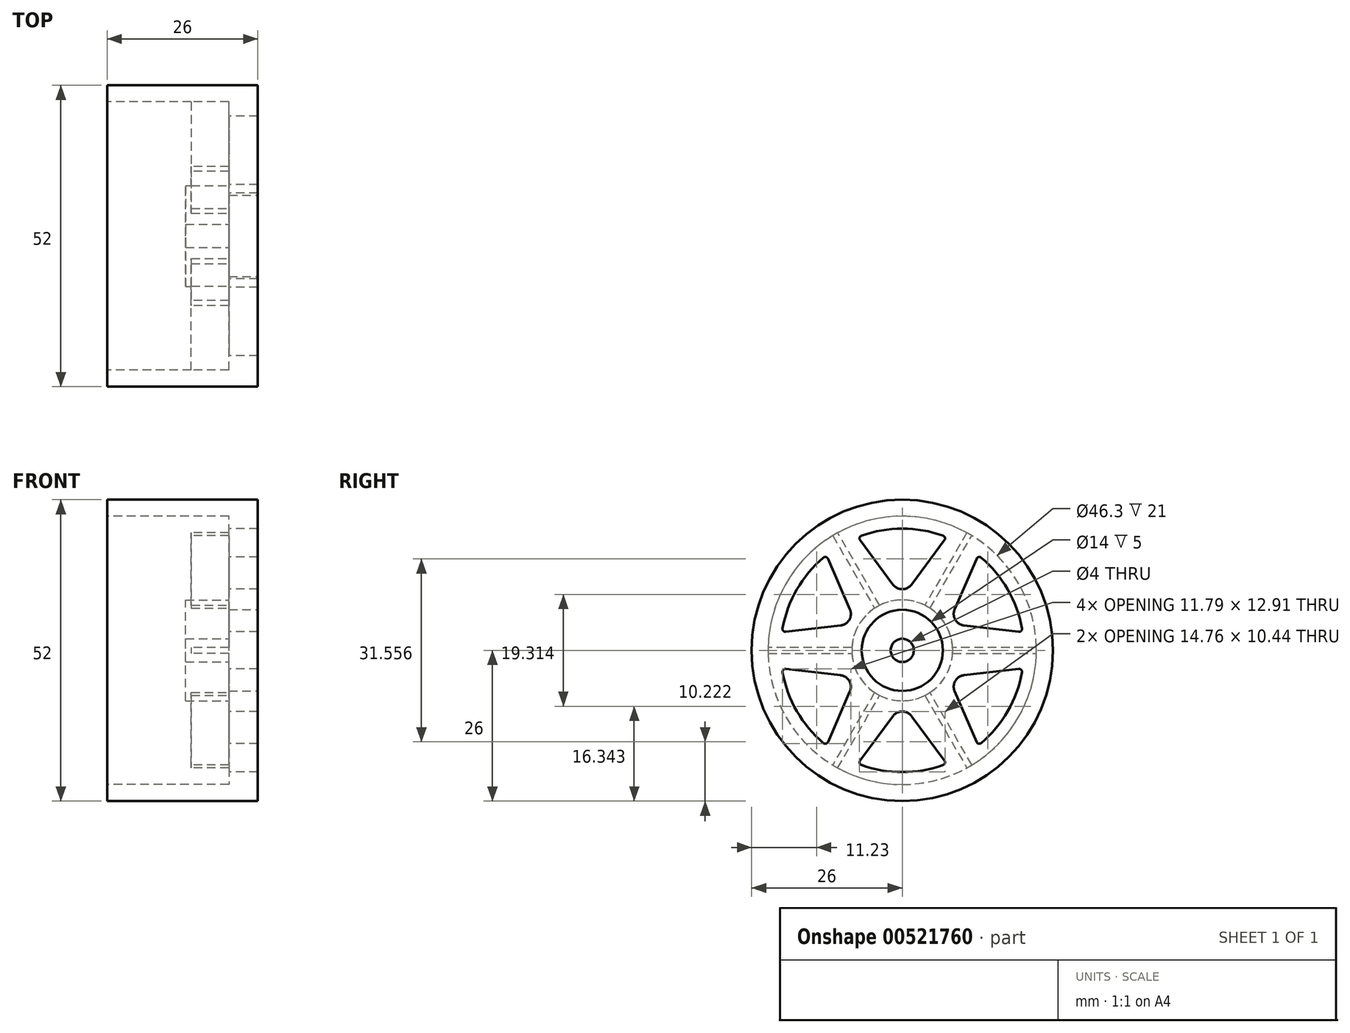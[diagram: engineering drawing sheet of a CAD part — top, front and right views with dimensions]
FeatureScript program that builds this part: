
annotation { "Feature Type Name" : "Feature", "Feature Type Description" : "" }
export const myFeature = defineFeature(function(context is Context, id is Id, definition is map)
    precondition{}
    {
        {
            var Q0;
            Q0=qCreatedBy(makeId("Right.planeOp"),FACE);
            var sketch = newSketch(context, id + "F0", { "sketchPlane" : qUnion([Q0])});
            skCircle(sketch, "E0", {"center": v(0, 0) * mm, "radius": 26 * mm});
            skSolve(sketch);
        }
        {
            var Q0;
            Q0 = qSketchRegion(id + "F0", true);
            extrude(context, id + "F1", {"entities" : qUnion([Q0]), "depth" : 26 * mm, "offsetDistance" : 25 * mm});
        }
        {
            var Q0;
            Q0=qCreatedBy(makeId("Right.planeOp"),FACE);
            cPlane(context, id + "F2", {"entities" : qUnion([Q0]), "cplaneType" : CPlaneType.OFFSET, "offset" : 26 * mm, "width" : 150 * mm, "height" : 150 * mm});
        }
        {
            var Q0;
            Q0=qCreatedBy(makeId("Right.planeOp"),FACE);
            var sketch = newSketch(context, id + "F3", { "sketchPlane" : qUnion([Q0])});
            skCircle(sketch, "E1", {"center": v(0, 0) * mm, "radius": 23.15 * mm});
            skSolve(sketch);
        }
        {
            var Q0;
            Q0=makeQuery(id+"F3.imprint","IMPRINT",FACE,{"disambiguationData":[TD([[makeQuery(id+"F3.imprint","IMPRINT",EDGE,{"derivedFrom":sQuery(id+"F3.wireOp",EDGE,"E1")}),1.0]])]});
            extrude(context, id + "F4", {"entities" : qUnion([Q0]), "operationType" : NewBodyOperationType.REMOVE, "depth" : 21 * mm, "offsetDistance" : 25 * mm});
        }
        {
            var Q0;
            Q0=qCreatedBy(id+"F2.planeOp",FACE);
            var sketch = newSketch(context, id + "F5", { "sketchPlane" : qUnion([Q0])});
            skCircle(sketch, "E2", {"center": v(0, 0) * mm, "radius": 8.7 * mm});
            skSolve(sketch);
        }
        {
            var Q0;
            Q0=makeQuery(id+"F5.imprint","IMPRINT",FACE,{"disambiguationData":[TD([[makeQuery(id+"F5.imprint","IMPRINT",EDGE,{"derivedFrom":sQuery(id+"F5.wireOp",EDGE,"E2")}),1.0]])]});
            extrude(context, id + "F6", {"entities" : qUnion([Q0]), "operationType" : NewBodyOperationType.ADD, "oppositeDirection" : true, "depth" : 12.5 * mm, "offsetDistance" : 25 * mm});
        }
        {
            var Q0;
            Q0=qCreatedBy(id+"F2.planeOp",FACE);
            var sketch = newSketch(context, id + "F7", { "sketchPlane" : qUnion([Q0])});
            skLineSegment(sketch, "E3", {"start": v(0, 9.2) * mm, "end": v(9, 21.33) * mm});
            skLineSegment(sketch, "E4", {"start": v(9, 21.33) * mm, "end": v(-9, 21.33) * mm});
            skLineSegment(sketch, "E5", {"start": v(-9, 21.33) * mm, "end": v(0, 9.2) * mm});
            skLineSegment(sketch, "E6.1.0", {"start": v(-7.97, 4.6) * mm, "end": v(-13.97, 18.46) * mm});
            skLineSegment(sketch, "E6.1.1", {"start": v(-13.97, 18.46) * mm, "end": v(-22.97, 2.87) * mm});
            skLineSegment(sketch, "E6.1.2", {"start": v(-22.97, 2.87) * mm, "end": v(-7.97, 4.6) * mm});
            skLineSegment(sketch, "E6.2.0", {"start": v(-7.97, -4.6) * mm, "end": v(-22.97, -2.87) * mm});
            skLineSegment(sketch, "E6.2.1", {"start": v(-22.97, -2.87) * mm, "end": v(-13.97, -18.46) * mm});
            skLineSegment(sketch, "E6.2.2", {"start": v(-13.97, -18.46) * mm, "end": v(-7.97, -4.6) * mm});
            skLineSegment(sketch, "E6.3.0", {"start": v(0, -9.2) * mm, "end": v(-9, -21.33) * mm});
            skLineSegment(sketch, "E6.3.1", {"start": v(-9, -21.33) * mm, "end": v(9, -21.33) * mm});
            skLineSegment(sketch, "E6.3.2", {"start": v(9, -21.33) * mm, "end": v(0, -9.2) * mm});
            skLineSegment(sketch, "E6.4.0", {"start": v(7.97, -4.6) * mm, "end": v(13.97, -18.46) * mm});
            skLineSegment(sketch, "E6.4.1", {"start": v(13.97, -18.46) * mm, "end": v(22.97, -2.87) * mm});
            skLineSegment(sketch, "E6.4.2", {"start": v(22.97, -2.87) * mm, "end": v(7.97, -4.6) * mm});
            skLineSegment(sketch, "E6.5.0", {"start": v(7.97, 4.6) * mm, "end": v(22.97, 2.87) * mm});
            skLineSegment(sketch, "E6.5.1", {"start": v(22.97, 2.87) * mm, "end": v(13.97, 18.46) * mm});
            skLineSegment(sketch, "E6.5.2", {"start": v(13.97, 18.46) * mm, "end": v(7.97, 4.6) * mm});
            skPoint(sketch, "E6.center", {"position": v(0, 0) * mm});
            skSolve(sketch);
        }
        {
            var Q0;
            Q0=makeQuery(id+"F7.imprint","IMPRINT",FACE,{"disambiguationData":[TD([[makeQuery(id+"F7.imprint","IMPRINT",EDGE,{"derivedFrom":sQuery(id+"F7.wireOp",EDGE,"E6.1.0")}),1.0]])]});
            var Q1;
            Q1=makeQuery(id+"F7.imprint","IMPRINT",FACE,{"disambiguationData":[TD([[makeQuery(id+"F7.imprint","IMPRINT",EDGE,{"derivedFrom":sQuery(id+"F7.wireOp",EDGE,"E3")}),1.0]])]});
            var Q2;
            Q2=makeQuery(id+"F7.imprint","IMPRINT",FACE,{"disambiguationData":[TD([[makeQuery(id+"F7.imprint","IMPRINT",EDGE,{"derivedFrom":sQuery(id+"F7.wireOp",EDGE,"E6.5.0")}),1.0]])]});
            var Q3;
            Q3=makeQuery(id+"F7.imprint","IMPRINT",FACE,{"disambiguationData":[TD([[makeQuery(id+"F7.imprint","IMPRINT",EDGE,{"derivedFrom":sQuery(id+"F7.wireOp",EDGE,"E6.4.0")}),1.0]])]});
            var Q4;
            Q4=makeQuery(id+"F7.imprint","IMPRINT",FACE,{"disambiguationData":[TD([[makeQuery(id+"F7.imprint","IMPRINT",EDGE,{"derivedFrom":sQuery(id+"F7.wireOp",EDGE,"E6.3.0")}),1.0]])]});
            var Q5;
            Q5=makeQuery(id+"F7.imprint","IMPRINT",FACE,{"disambiguationData":[TD([[makeQuery(id+"F7.imprint","IMPRINT",EDGE,{"derivedFrom":sQuery(id+"F7.wireOp",EDGE,"E6.2.0")}),1.0]])]});
            extrude(context, id + "F8", {"entities" : qUnion([Q0, Q1, Q2, Q3, Q4, Q5]), "operationType" : NewBodyOperationType.REMOVE, "oppositeDirection" : true, "depth" : 25 * mm, "offsetDistance" : 25 * mm});
        }
        {
            var Q0;
            Q0=qCreatedBy(id+"F2.planeOp",FACE);
            var sketch = newSketch(context, id + "F9", { "sketchPlane" : qUnion([Q0])});
            skCircle(sketch, "E7", {"center": v(0, 0) * mm, "radius": 7 * mm});
            skSolve(sketch);
        }
        {
            var Q0;
            Q0=makeQuery(id+"F9.imprint","IMPRINT",FACE,{"disambiguationData":[TD([[makeQuery(id+"F9.imprint","IMPRINT",EDGE,{"derivedFrom":sQuery(id+"F9.wireOp",EDGE,"E7")}),1.0]])]});
            extrude(context, id + "F10", {"entities" : qUnion([Q0]), "operationType" : NewBodyOperationType.REMOVE, "oppositeDirection" : true, "depth" : 5 * mm, "offsetDistance" : 25 * mm});
        }
        {
            var Q0;
            Q0=qCreatedBy(id+"F2.planeOp",FACE);
            var sketch = newSketch(context, id + "F11", { "sketchPlane" : qUnion([Q0])});
            skCircle(sketch, "E8", {"center": v(0, 0) * mm, "radius": 2 * mm});
            skSolve(sketch);
        }
        {
            var Q0;
            Q0=makeQuery(id+"F11.imprint","IMPRINT",FACE,{"disambiguationData":[TD([[makeQuery(id+"F11.imprint","IMPRINT",EDGE,{"derivedFrom":sQuery(id+"F11.wireOp",EDGE,"E8")}),1.0]])]});
            extrude(context, id + "F12", {"entities" : qUnion([Q0]), "operationType" : NewBodyOperationType.REMOVE, "oppositeDirection" : true, "depth" : 25 * mm, "offsetDistance" : 25 * mm});
        }
        {
            var Q0;
            Q0=qCreatedBy(makeId("Front.planeOp"),FACE);
            var sketch = newSketch(context, id + "F13", { "sketchPlane" : qUnion([Q0])});
            skLineSegment(sketch, "E9.bottom", {"start": v(21, 25.11) * mm, "end": v(26, 25.11) * mm});
            skLineSegment(sketch, "E9.top", {"start": v(21, 21) * mm, "end": v(26, 21) * mm});
            skLineSegment(sketch, "E9.left", {"start": v(21, 25.11) * mm, "end": v(21, 21) * mm});
            skLineSegment(sketch, "E9.right", {"start": v(26, 25.11) * mm, "end": v(26, 21) * mm});
            skLineSegment(sketch, "E10", {"start": v(-12.19, 0) * mm, "end": v(38.5, 0) * mm, "construction": true});
            skSolve(sketch);
        }
        {
            var Q0;
            Q0 = qSketchRegion(id + "F13", true);
            var Q1;
            Q1=sQuery(id+"F13.wireOp",EDGE,"E10");
            revolve(context, id + "F14", {"operationType" : NewBodyOperationType.ADD, "entities" : qUnion([Q0]), "axis" : qUnion([Q1]), "revolveType" : RevolveType.FULL});
        }
        {
            var Q0;
            Q0=qCreatedBy(makeId("Right.planeOp"),FACE);
            var sketch = newSketch(context, id + "F15", { "sketchPlane" : qUnion([Q0])});
            skLineSegment(sketch, "E11", {"start": v(5.86, 10.14) * mm, "end": v(0, 0) * mm, "construction": true});
            skLineSegment(sketch, "E12", {"start": v(12.5, 21.65) * mm, "end": v(12.93, 21.4) * mm});
            skLineSegment(sketch, "E13", {"start": v(12.93, 21.4) * mm, "end": v(4.43, 6.68) * mm});
            skLineSegment(sketch, "E14", {"start": v(4.43, 6.68) * mm, "end": v(3.57, 7.18) * mm});
            skLineSegment(sketch, "E15", {"start": v(3.57, 7.18) * mm, "end": v(12.07, 21.9) * mm});
            skLineSegment(sketch, "E16", {"start": v(12.07, 21.9) * mm, "end": v(12.5, 21.65) * mm});
            skLineSegment(sketch, "E17.1.0", {"start": v(-12.07, 21.9) * mm, "end": v(-3.57, 7.18) * mm});
            skLineSegment(sketch, "E17.1.1", {"start": v(-3.57, 7.18) * mm, "end": v(-4.43, 6.68) * mm});
            skLineSegment(sketch, "E17.1.2", {"start": v(-4.43, 6.68) * mm, "end": v(-12.93, 21.4) * mm});
            skLineSegment(sketch, "E17.1.3", {"start": v(-12.93, 21.4) * mm, "end": v(-12.5, 21.65) * mm});
            skLineSegment(sketch, "E17.1.4", {"start": v(-12.5, 21.65) * mm, "end": v(-12.07, 21.9) * mm});
            skLineSegment(sketch, "E17.2.0", {"start": v(-25, 0.5) * mm, "end": v(-8, 0.5) * mm});
            skLineSegment(sketch, "E17.2.1", {"start": v(-8, 0.5) * mm, "end": v(-8, -0.5) * mm});
            skLineSegment(sketch, "E17.2.2", {"start": v(-8, -0.5) * mm, "end": v(-25, -0.5) * mm});
            skLineSegment(sketch, "E17.2.3", {"start": v(-25, -0.5) * mm, "end": v(-25, 0) * mm});
            skLineSegment(sketch, "E17.2.4", {"start": v(-25, 0) * mm, "end": v(-25, 0.5) * mm});
            skLineSegment(sketch, "E17.3.0", {"start": v(-12.93, -21.4) * mm, "end": v(-4.43, -6.68) * mm});
            skLineSegment(sketch, "E17.3.1", {"start": v(-4.43, -6.68) * mm, "end": v(-3.57, -7.18) * mm});
            skLineSegment(sketch, "E17.3.2", {"start": v(-3.57, -7.18) * mm, "end": v(-12.07, -21.9) * mm});
            skLineSegment(sketch, "E17.3.3", {"start": v(-12.07, -21.9) * mm, "end": v(-12.5, -21.65) * mm});
            skLineSegment(sketch, "E17.3.4", {"start": v(-12.5, -21.65) * mm, "end": v(-12.93, -21.4) * mm});
            skLineSegment(sketch, "E17.4.0", {"start": v(12.07, -21.9) * mm, "end": v(3.57, -7.18) * mm});
            skLineSegment(sketch, "E17.4.1", {"start": v(3.57, -7.18) * mm, "end": v(4.43, -6.68) * mm});
            skLineSegment(sketch, "E17.4.2", {"start": v(4.43, -6.68) * mm, "end": v(12.93, -21.4) * mm});
            skLineSegment(sketch, "E17.4.3", {"start": v(12.93, -21.4) * mm, "end": v(12.5, -21.65) * mm});
            skLineSegment(sketch, "E17.4.4", {"start": v(12.5, -21.65) * mm, "end": v(12.07, -21.9) * mm});
            skLineSegment(sketch, "E17.5.0", {"start": v(25, -0.5) * mm, "end": v(8, -0.5) * mm});
            skLineSegment(sketch, "E17.5.1", {"start": v(8, -0.5) * mm, "end": v(8, 0.5) * mm});
            skLineSegment(sketch, "E17.5.2", {"start": v(8, 0.5) * mm, "end": v(25, 0.5) * mm});
            skLineSegment(sketch, "E17.5.3", {"start": v(25, 0.5) * mm, "end": v(25, 0) * mm});
            skLineSegment(sketch, "E17.5.4", {"start": v(25, 0) * mm, "end": v(25, -0.5) * mm});
            skPoint(sketch, "E17.center", {"position": v(0, 0) * mm});
            skSolve(sketch);
        }
        {
            var Q0;
            Q0 = qSketchRegion(id + "F15", true);
            extrude(context, id + "F16", {"entities" : qUnion([Q0]), "operationType" : NewBodyOperationType.ADD, "depth" : 25 * mm, "offsetDistance" : 25 * mm});
        }
        {
            var Q0;
            Q0=qCreatedBy(makeId("Front.planeOp"),FACE);
            var sketch = newSketch(context, id + "F17", { "sketchPlane" : qUnion([Q0])});
            skLineSegment(sketch, "E18", {"start": v(-3.07, 23.15) * mm, "end": v(-1.8, 5.68) * mm});
            skLineSegment(sketch, "E19", {"start": v(-1.8, 5.68) * mm, "end": v(13.5, 5.68) * mm});
            skLineSegment(sketch, "E20", {"start": v(13.5, 5.68) * mm, "end": v(13.5, 8.7) * mm});
            skLineSegment(sketch, "E21", {"start": v(13.5, 8.7) * mm, "end": v(14.5, 8.7) * mm});
            skLineSegment(sketch, "E22", {"start": v(14.5, 8.7) * mm, "end": v(14.5, 23.15) * mm});
            skLineSegment(sketch, "E23", {"start": v(14.5, 23.15) * mm, "end": v(-3.07, 23.15) * mm});
            skLineSegment(sketch, "E24", {"start": v(-26.71, 0) * mm, "end": v(46.58, 0) * mm, "construction": true});
            skSolve(sketch);
        }
        {
            var Q0;
            Q0 = qSketchRegion(id + "F17", true);
            var Q1;
            Q1=sQuery(id+"F17.wireOp",EDGE,"E24");
            revolve(context, id + "F18", {"operationType" : NewBodyOperationType.REMOVE, "entities" : qUnion([Q0]), "axis" : qUnion([Q1]), "revolveType" : RevolveType.FULL, "oppositeDirection" : true});
        }
        {
            var Q0;
            Q0=makeQuery(id+"F8.boolean.opBoolean","COPY",EDGE,{"derivedFrom":makeQuery(id+"F8.opExtrude","SWEPT_EDGE",EDGE,{"disambiguationData":[OSD([sQuery(id+"F7.wireOp",EDGE,"E6.1.0"),sQuery(id+"F7.wireOp",EDGE,"E6.1.2")])]})});
            var Q1;
            Q1=makeQuery(id+"F8.boolean.opBoolean","COPY",EDGE,{"derivedFrom":makeQuery(id+"F8.opExtrude","SWEPT_EDGE",EDGE,{"disambiguationData":[OSD([sQuery(id+"F7.wireOp",EDGE,"E3"),sQuery(id+"F7.wireOp",EDGE,"E5")])]})});
            var Q2;
            Q2=makeQuery(id+"F8.boolean.opBoolean","COPY",EDGE,{"derivedFrom":makeQuery(id+"F8.opExtrude","SWEPT_EDGE",EDGE,{"disambiguationData":[OSD([sQuery(id+"F7.wireOp",EDGE,"E6.5.0"),sQuery(id+"F7.wireOp",EDGE,"E6.5.2")])]})});
            var Q3;
            Q3=makeQuery(id+"F8.boolean.opBoolean","COPY",EDGE,{"derivedFrom":makeQuery(id+"F8.opExtrude","SWEPT_EDGE",EDGE,{"disambiguationData":[OSD([sQuery(id+"F7.wireOp",EDGE,"E6.4.0"),sQuery(id+"F7.wireOp",EDGE,"E6.4.2")])]})});
            var Q4;
            Q4=makeQuery(id+"F8.boolean.opBoolean","COPY",EDGE,{"derivedFrom":makeQuery(id+"F8.opExtrude","SWEPT_EDGE",EDGE,{"disambiguationData":[OSD([sQuery(id+"F7.wireOp",EDGE,"E6.3.0"),sQuery(id+"F7.wireOp",EDGE,"E6.3.2")])]})});
            var Q5;
            Q5=makeQuery(id+"F8.boolean.opBoolean","COPY",EDGE,{"derivedFrom":makeQuery(id+"F8.opExtrude","SWEPT_EDGE",EDGE,{"disambiguationData":[OSD([sQuery(id+"F7.wireOp",EDGE,"E6.2.0"),sQuery(id+"F7.wireOp",EDGE,"E6.2.2")])]})});
            fillet(context, id + "F19", {"entities" : qUnion([Q0, Q1, Q2, Q3, Q4, Q5]), "radius" : 2 * mm, "tangentPropagation" : true, "allowEdgeOverflow" : false});
        }
        {
            var Q0;
            Q0=makeQuery(id+"F14.boolean.opBoolean","INTERSECT",EDGE,{"derivedFrom":[makeQuery(id+"F8.boolean.opBoolean","COPY",FACE,{"derivedFrom":makeQuery(id+"F8.opExtrude","SWEPT_FACE",FACE,{"disambiguationData":[OSD([sQuery(id+"F7.wireOp",EDGE,"E6.4.2")])]})}),makeQuery(id+"F14.opRevolve","SWEPT_FACE",FACE,{"disambiguationData":[OSD([sQuery(id+"F13.wireOp",EDGE,"E9.top")])]})]});
            var Q1;
            Q1=makeQuery(id+"F14.boolean.opBoolean","INTERSECT",EDGE,{"derivedFrom":[makeQuery(id+"F8.boolean.opBoolean","COPY",FACE,{"derivedFrom":makeQuery(id+"F8.opExtrude","SWEPT_FACE",FACE,{"disambiguationData":[OSD([sQuery(id+"F7.wireOp",EDGE,"E6.4.0")])]})}),makeQuery(id+"F14.opRevolve","SWEPT_FACE",FACE,{"disambiguationData":[OSD([sQuery(id+"F13.wireOp",EDGE,"E9.top")])]})]});
            var Q2;
            Q2=makeQuery(id+"F14.boolean.opBoolean","INTERSECT",EDGE,{"derivedFrom":[makeQuery(id+"F8.boolean.opBoolean","COPY",FACE,{"derivedFrom":makeQuery(id+"F8.opExtrude","SWEPT_FACE",FACE,{"disambiguationData":[OSD([sQuery(id+"F7.wireOp",EDGE,"E6.5.0")])]})}),makeQuery(id+"F14.opRevolve","SWEPT_FACE",FACE,{"disambiguationData":[OSD([sQuery(id+"F13.wireOp",EDGE,"E9.top")])]})]});
            var Q3;
            Q3=makeQuery(id+"F14.boolean.opBoolean","INTERSECT",EDGE,{"derivedFrom":[makeQuery(id+"F8.boolean.opBoolean","COPY",FACE,{"derivedFrom":makeQuery(id+"F8.opExtrude","SWEPT_FACE",FACE,{"disambiguationData":[OSD([sQuery(id+"F7.wireOp",EDGE,"E6.5.2")])]})}),makeQuery(id+"F14.opRevolve","SWEPT_FACE",FACE,{"disambiguationData":[OSD([sQuery(id+"F13.wireOp",EDGE,"E9.top")])]})]});
            var Q4;
            Q4=makeQuery(id+"F14.boolean.opBoolean","INTERSECT",EDGE,{"derivedFrom":[makeQuery(id+"F8.boolean.opBoolean","COPY",FACE,{"derivedFrom":makeQuery(id+"F8.opExtrude","SWEPT_FACE",FACE,{"disambiguationData":[OSD([sQuery(id+"F7.wireOp",EDGE,"E6.3.2")])]})}),makeQuery(id+"F14.opRevolve","SWEPT_FACE",FACE,{"disambiguationData":[OSD([sQuery(id+"F13.wireOp",EDGE,"E9.top")])]})]});
            var Q5;
            Q5=makeQuery(id+"F14.boolean.opBoolean","INTERSECT",EDGE,{"derivedFrom":[makeQuery(id+"F8.boolean.opBoolean","COPY",FACE,{"derivedFrom":makeQuery(id+"F8.opExtrude","SWEPT_FACE",FACE,{"disambiguationData":[OSD([sQuery(id+"F7.wireOp",EDGE,"E3")])]})}),makeQuery(id+"F14.opRevolve","SWEPT_FACE",FACE,{"disambiguationData":[OSD([sQuery(id+"F13.wireOp",EDGE,"E9.top")])]})]});
            var Q6;
            Q6=makeQuery(id+"F14.boolean.opBoolean","INTERSECT",EDGE,{"derivedFrom":[makeQuery(id+"F8.boolean.opBoolean","COPY",FACE,{"derivedFrom":makeQuery(id+"F8.opExtrude","SWEPT_FACE",FACE,{"disambiguationData":[OSD([sQuery(id+"F7.wireOp",EDGE,"E5")])]})}),makeQuery(id+"F14.opRevolve","SWEPT_FACE",FACE,{"disambiguationData":[OSD([sQuery(id+"F13.wireOp",EDGE,"E9.top")])]})]});
            var Q7;
            Q7=makeQuery(id+"F14.boolean.opBoolean","INTERSECT",EDGE,{"derivedFrom":[makeQuery(id+"F8.boolean.opBoolean","COPY",FACE,{"derivedFrom":makeQuery(id+"F8.opExtrude","SWEPT_FACE",FACE,{"disambiguationData":[OSD([sQuery(id+"F7.wireOp",EDGE,"E6.1.0")])]})}),makeQuery(id+"F14.opRevolve","SWEPT_FACE",FACE,{"disambiguationData":[OSD([sQuery(id+"F13.wireOp",EDGE,"E9.top")])]})]});
            var Q8;
            Q8=makeQuery(id+"F14.boolean.opBoolean","INTERSECT",EDGE,{"derivedFrom":[makeQuery(id+"F8.boolean.opBoolean","COPY",FACE,{"derivedFrom":makeQuery(id+"F8.opExtrude","SWEPT_FACE",FACE,{"disambiguationData":[OSD([sQuery(id+"F7.wireOp",EDGE,"E6.1.2")])]})}),makeQuery(id+"F14.opRevolve","SWEPT_FACE",FACE,{"disambiguationData":[OSD([sQuery(id+"F13.wireOp",EDGE,"E9.top")])]})]});
            var Q9;
            Q9=makeQuery(id+"F14.boolean.opBoolean","INTERSECT",EDGE,{"derivedFrom":[makeQuery(id+"F8.boolean.opBoolean","COPY",FACE,{"derivedFrom":makeQuery(id+"F8.opExtrude","SWEPT_FACE",FACE,{"disambiguationData":[OSD([sQuery(id+"F7.wireOp",EDGE,"E6.2.0")])]})}),makeQuery(id+"F14.opRevolve","SWEPT_FACE",FACE,{"disambiguationData":[OSD([sQuery(id+"F13.wireOp",EDGE,"E9.top")])]})]});
            var Q10;
            Q10=makeQuery(id+"F14.boolean.opBoolean","INTERSECT",EDGE,{"derivedFrom":[makeQuery(id+"F8.boolean.opBoolean","COPY",FACE,{"derivedFrom":makeQuery(id+"F8.opExtrude","SWEPT_FACE",FACE,{"disambiguationData":[OSD([sQuery(id+"F7.wireOp",EDGE,"E6.2.2")])]})}),makeQuery(id+"F14.opRevolve","SWEPT_FACE",FACE,{"disambiguationData":[OSD([sQuery(id+"F13.wireOp",EDGE,"E9.top")])]})]});
            var Q11;
            Q11=makeQuery(id+"F14.boolean.opBoolean","INTERSECT",EDGE,{"derivedFrom":[makeQuery(id+"F8.boolean.opBoolean","COPY",FACE,{"derivedFrom":makeQuery(id+"F8.opExtrude","SWEPT_FACE",FACE,{"disambiguationData":[OSD([sQuery(id+"F7.wireOp",EDGE,"E6.3.0")])]})}),makeQuery(id+"F14.opRevolve","SWEPT_FACE",FACE,{"disambiguationData":[OSD([sQuery(id+"F13.wireOp",EDGE,"E9.top")])]})]});
            fillet(context, id + "F20", {"entities" : qUnion([Q0, Q1, Q2, Q3, Q4, Q5, Q6, Q7, Q8, Q9, Q10, Q11]), "radius" : 0.5 * mm, "tangentPropagation" : true, "allowEdgeOverflow" : false});
        }
    });
